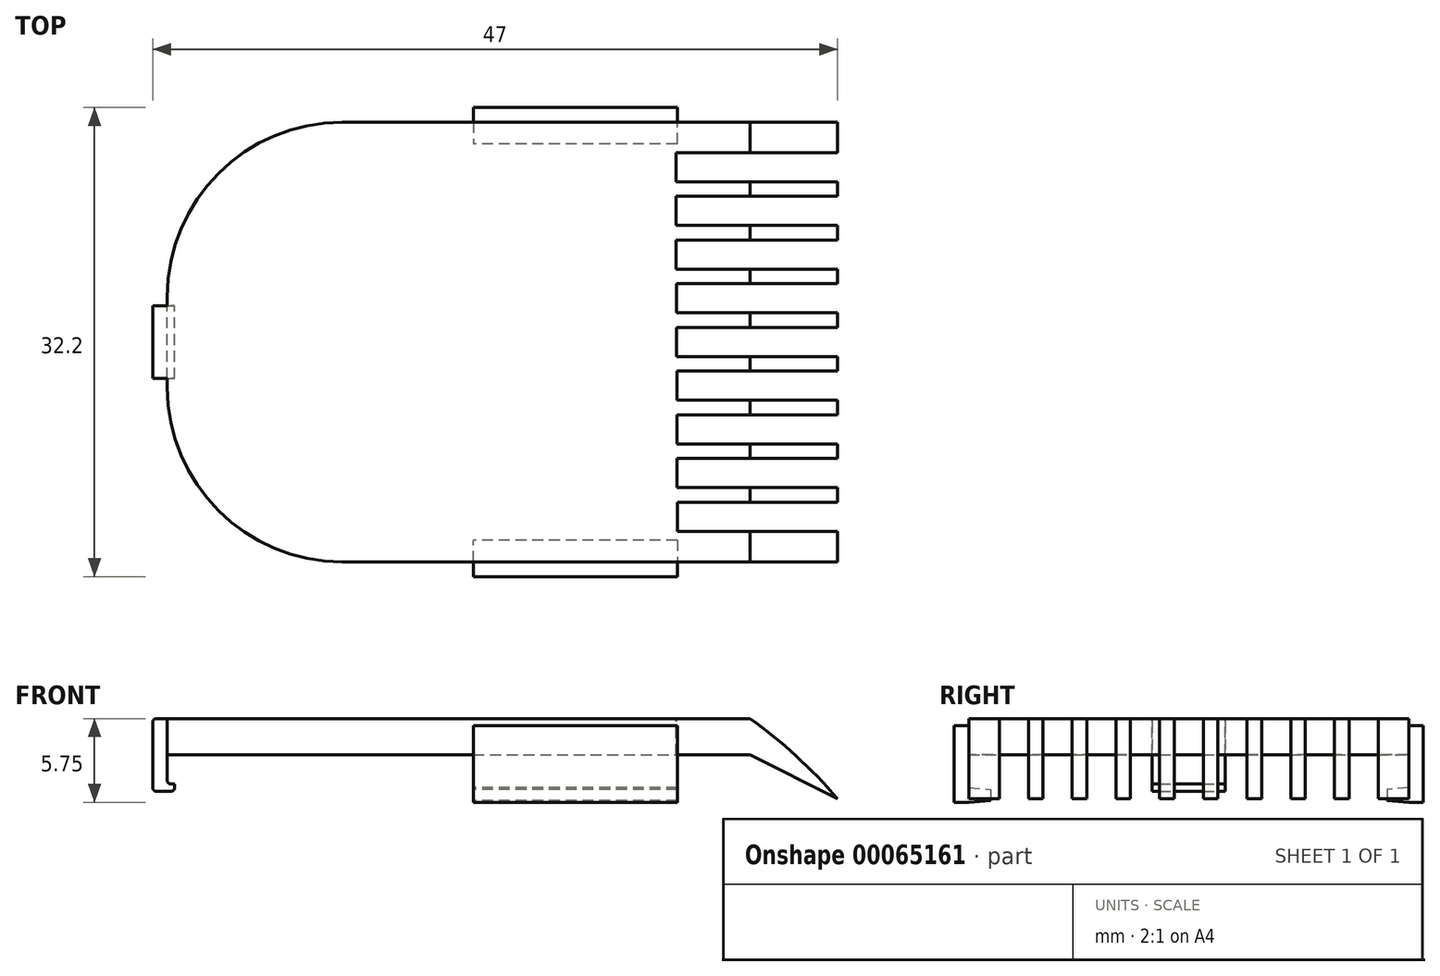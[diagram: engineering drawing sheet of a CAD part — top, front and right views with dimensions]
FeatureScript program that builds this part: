
annotation { "Feature Type Name" : "Feature", "Feature Type Description" : "" }
export const myFeature = defineFeature(function(context is Context, id is Id, definition is map)
    precondition{}
    {
        {
            var Q0;
            Q0=qCreatedBy(makeId("Front.planeOp"),FACE);
            var sketch = newSketch(context, id + "F0", { "sketchPlane" : qUnion([Q0])});
            skLineSegment(sketch, "E0", {"start": v(-71.46, 38.2) * mm, "end": v(-31.46, 38.2) * mm});
            skLineSegment(sketch, "E1", {"start": v(-31.46, 38.2) * mm, "end": v(-25.46, 35.2) * mm});
            skLineSegment(sketch, "E2", {"start": v(-71.46, 38.2) * mm, "end": v(-71.46, 40.7) * mm});
            skLineSegment(sketch, "E3", {"start": v(-71.46, 40.7) * mm, "end": v(-31.46, 40.7) * mm});
            skArc(sketch, "E4", {"start": v(-25.46, 35.2) * mm, "mid": v(-28.3, 38.13) * mm, "end": v(-31.46, 40.7) * mm});
            skLineSegment(sketch, "E5", {"start": v(-71.46, 40.7) * mm, "end": v(-72.21, 40.7) * mm});
            skLineSegment(sketch, "E6", {"start": v(-72.46, 40.45) * mm, "end": v(-72.46, 35.95) * mm});
            skLineSegment(sketch, "E7", {"start": v(-72.21, 35.7) * mm, "end": v(-71.21, 35.7) * mm});
            skLineSegment(sketch, "E8", {"start": v(-70.96, 35.95) * mm, "end": v(-70.96, 36.2) * mm});
            skLineSegment(sketch, "E9", {"start": v(-70.96, 36.2) * mm, "end": v(-71.21, 36.2) * mm});
            skLineSegment(sketch, "E10", {"start": v(-71.46, 36.45) * mm, "end": v(-71.46, 38.2) * mm});
            skPoint(sketch, "E11.visualSharp", {"position": v(-72.46, 40.7) * mm});
            skArc(sketch, "E11.filletArc", {"start": v(-72.21, 40.7) * mm, "mid": v(-72.39, 40.63) * mm, "end": v(-72.46, 40.45) * mm});
            skPoint(sketch, "E12.visualSharp", {"position": v(-72.46, 35.7) * mm});
            skArc(sketch, "E12.filletArc", {"start": v(-72.46, 35.95) * mm, "mid": v(-72.39, 35.77) * mm, "end": v(-72.21, 35.7) * mm});
            skPoint(sketch, "E13.visualSharp", {"position": v(-71.46, 36.2) * mm});
            skArc(sketch, "E13.filletArc", {"start": v(-71.46, 36.45) * mm, "mid": v(-71.39, 36.27) * mm, "end": v(-71.21, 36.2) * mm});
            skPoint(sketch, "E14.visualSharp", {"position": v(-70.96, 35.7) * mm});
            skArc(sketch, "E14.filletArc", {"start": v(-71.21, 35.7) * mm, "mid": v(-71.03, 35.77) * mm, "end": v(-70.96, 35.95) * mm});
            skSolve(sketch);
        }
        {
            var Q0;
            Q0=makeQuery(id+"F0.imprint","IMPRINT",FACE,{"disambiguationData":[TD([[makeQuery(id+"F0.imprint","IMPRINT",EDGE,{"derivedFrom":sQuery(id+"F0.wireOp",EDGE,"E0")}),1.0]])]});
            extrude(context, id + "F1", {"entities" : qUnion([Q0]), "depth" : 15.1 * mm, "hasSecondDirection" : true, "secondDirectionOppositeDirection" : true, "secondDirectionDepth" : 15.1 * mm});
        }
        {
            var Q0;
            Q0=makeQuery(id+"F0.imprint","IMPRINT",FACE,{"disambiguationData":[TD([[makeQuery(id+"F0.imprint","IMPRINT",EDGE,{"derivedFrom":sQuery(id+"F0.wireOp",EDGE,"E2")}),1.0]])]});
            extrude(context, id + "F2", {"entities" : qUnion([Q0]), "operationType" : NewBodyOperationType.ADD, "depth" : 2.5 * mm, "hasSecondDirection" : true, "secondDirectionOppositeDirection" : true, "secondDirectionDepth" : 2.5 * mm});
        }
        {
            var Q0;
            Q0=makeQuery(id+"F1.opExtrude","SWEPT_FACE",FACE,{"disambiguationData":[OSD([sQuery(id+"F0.wireOp",EDGE,"E0")])]});
            var sketch = newSketch(context, id + "F3", { "sketchPlane" : qUnion([Q0])});
            skLineSegment(sketch, "E15", {"start": v(-50.46, -15.1) * mm, "end": v(-50.46, -16.1) * mm});
            skLineSegment(sketch, "E16", {"start": v(-50.46, -16.1) * mm, "end": v(-36.46, -16.1) * mm});
            skLineSegment(sketch, "E17", {"start": v(-36.46, -16.1) * mm, "end": v(-36.46, -15.1) * mm});
            skLineSegment(sketch, "E18", {"start": v(-36.46, -15.1) * mm, "end": v(-50.46, -15.1) * mm});
            skSolve(sketch);
        }
        {
            var Q0;
            {var subQ0=sQuery(id+"F3.wireOp",EDGE,"E15");Q0=makeQuery(id+"F3.imprint","IMPRINT",FACE,{"disambiguationData":[TD([[makeQuery(id+"F3.imprint","IMPRINT",EDGE,{"derivedFrom":subQ0}),1.0]])]});}
            extrude(context, id + "F4", {"entities" : qUnion([Q0]), "oppositeDirection" : true, "depth" : 2 * mm, "hasSecondDirection" : true, "secondDirectionOppositeDirection" : false, "secondDirectionDepth" : 4 * mm});
        }
        {
            var Q0;
            Q0=makeQuery(id+"F4.opExtrude","SWEPT_FACE",FACE,{"disambiguationData":[OSD([sQuery(id+"F3.wireOp",EDGE,"E18")])]});
            var sketch = newSketch(context, id + "F5", { "sketchPlane" : qUnion([Q0])});
            skLineSegment(sketch, "E19", {"start": v(-36.46, 35.95) * mm, "end": v(-50.46, 35.95) * mm});
            skPoint(sketch, "E19.endSnap0", {"position": v(-50.46, 37.2) * mm});
            skLineSegment(sketch, "E20", {"start": v(-43.46, 35.95) * mm, "end": v(-44.46, 34.2) * mm});
            skSolve(sketch);
        }
        {
            var Q0;
            {var subQ0=sQuery(id+"F5.wireOp",EDGE,"E19");Q0=makeQuery(id+"F5.imprint","IMPRINT",FACE,{"disambiguationData":[TD([[makeQuery(id+"F5.imprint","IMPRINT",EDGE,{"derivedFrom":subQ0}),1.0]])]});}
            extrude(context, id + "F6", {"entities" : qUnion([Q0]), "operationType" : NewBodyOperationType.ADD, "depth" : 1.5 * mm});
        }
        {
            var Q0;
            Q0=makeQuery(id+"F2.boolean.opBoolean","MERGE",FACE,{"derivedFrom":[makeQuery(id+"F1.opExtrude","SWEPT_FACE",FACE,{"disambiguationData":[OSD([sQuery(id+"F0.wireOp",EDGE,"E3")])]}),makeQuery(id+"F2.opExtrude","SWEPT_FACE",FACE,{"disambiguationData":[OSD([sQuery(id+"F0.wireOp",EDGE,"E5")])]})]});
            var sketch = newSketch(context, id + "F7", { "sketchPlane" : qUnion([Q0])});
            skLineSegment(sketch, "E21", {"start": v(-23.75, 13) * mm, "end": v(-36.55, 13) * mm});
            skLineSegment(sketch, "E22", {"start": v(-36.55, 13) * mm, "end": v(-36.55, 11) * mm});
            skLineSegment(sketch, "E23", {"start": v(-36.55, 11) * mm, "end": v(-23.68, 11) * mm});
            skLineSegment(sketch, "E24", {"start": v(-23.68, 11) * mm, "end": v(-23.75, 13) * mm});
            skLineSegment(sketch, "E25.1.0.0", {"start": v(-36.54, 8) * mm, "end": v(-23.67, 8) * mm});
            skLineSegment(sketch, "E25.1.0.1", {"start": v(-23.74, 10) * mm, "end": v(-36.54, 10) * mm});
            skLineSegment(sketch, "E25.1.0.2", {"start": v(-36.54, 10) * mm, "end": v(-36.54, 8) * mm});
            skLineSegment(sketch, "E25.1.0.3", {"start": v(-23.67, 8) * mm, "end": v(-23.74, 10) * mm});
            skLineSegment(sketch, "E25.2.0.0", {"start": v(-36.53, 5) * mm, "end": v(-23.66, 5) * mm});
            skLineSegment(sketch, "E25.2.0.1", {"start": v(-23.72, 7) * mm, "end": v(-36.53, 7) * mm});
            skLineSegment(sketch, "E25.2.0.2", {"start": v(-36.53, 7) * mm, "end": v(-36.53, 5) * mm});
            skLineSegment(sketch, "E25.2.0.3", {"start": v(-23.66, 5) * mm, "end": v(-23.72, 7) * mm});
            skLineSegment(sketch, "E25.3.0.0", {"start": v(-36.52, 2) * mm, "end": v(-23.65, 2) * mm});
            skLineSegment(sketch, "E25.3.0.1", {"start": v(-23.71, 4) * mm, "end": v(-36.52, 4) * mm});
            skLineSegment(sketch, "E25.3.0.2", {"start": v(-36.52, 4) * mm, "end": v(-36.52, 2) * mm});
            skLineSegment(sketch, "E25.3.0.3", {"start": v(-23.65, 2) * mm, "end": v(-23.71, 4) * mm});
            skLineSegment(sketch, "E25.4.0.0", {"start": v(-36.5, -1) * mm, "end": v(-23.64, -1) * mm});
            skLineSegment(sketch, "E25.4.0.1", {"start": v(-23.7, 1) * mm, "end": v(-36.5, 1) * mm});
            skLineSegment(sketch, "E25.4.0.2", {"start": v(-36.5, 1) * mm, "end": v(-36.5, -1) * mm});
            skLineSegment(sketch, "E25.4.0.3", {"start": v(-23.64, -1) * mm, "end": v(-23.7, 1) * mm});
            skLineSegment(sketch, "E25.5.0.0", {"start": v(-36.5, -4) * mm, "end": v(-23.63, -4) * mm});
            skLineSegment(sketch, "E25.5.0.1", {"start": v(-23.69, -2) * mm, "end": v(-36.5, -2) * mm});
            skLineSegment(sketch, "E25.5.0.2", {"start": v(-36.5, -2) * mm, "end": v(-36.5, -4) * mm});
            skLineSegment(sketch, "E25.5.0.3", {"start": v(-23.63, -4) * mm, "end": v(-23.69, -2) * mm});
            skLineSegment(sketch, "E25.6.0.0", {"start": v(-36.48, -7) * mm, "end": v(-23.61, -7) * mm});
            skLineSegment(sketch, "E25.6.0.1", {"start": v(-23.68, -5) * mm, "end": v(-36.48, -5) * mm});
            skLineSegment(sketch, "E25.6.0.2", {"start": v(-36.48, -5) * mm, "end": v(-36.48, -7) * mm});
            skLineSegment(sketch, "E25.6.0.3", {"start": v(-23.61, -7) * mm, "end": v(-23.68, -5) * mm});
            skLineSegment(sketch, "E25.7.0.0", {"start": v(-36.47, -10) * mm, "end": v(-23.6, -10) * mm});
            skLineSegment(sketch, "E25.7.0.1", {"start": v(-23.67, -8) * mm, "end": v(-36.47, -8) * mm});
            skLineSegment(sketch, "E25.7.0.2", {"start": v(-36.47, -8) * mm, "end": v(-36.47, -10) * mm});
            skLineSegment(sketch, "E25.7.0.3", {"start": v(-23.6, -10) * mm, "end": v(-23.67, -8) * mm});
            skLineSegment(sketch, "E25.8.0.0", {"start": v(-36.46, -13) * mm, "end": v(-23.6, -13) * mm});
            skLineSegment(sketch, "E25.8.0.1", {"start": v(-23.65, -11) * mm, "end": v(-36.46, -11) * mm});
            skLineSegment(sketch, "E25.8.0.2", {"start": v(-36.46, -11) * mm, "end": v(-36.46, -13) * mm});
            skLineSegment(sketch, "E25.8.0.3", {"start": v(-23.6, -13) * mm, "end": v(-23.65, -11) * mm});
            skLineSegment(sketch, "E25.direction1", {"start": v(-36.55, 11) * mm, "end": v(-36.54, 8) * mm, "construction": true});
            skSolve(sketch);
        }
        {
            var Q0;
            {var subQ0=sQuery(id+"F7.wireOp",EDGE,"E25.8.0.3");Q0=makeQuery(id+"F7.imprint","IMPRINT",FACE,{"disambiguationData":[TD([[makeQuery(id+"F7.imprint","IMPRINT",EDGE,{"derivedFrom":subQ0}),1.0]])]});}
            var Q1;
            {var subQ0=sQuery(id+"F7.wireOp",EDGE,"E25.7.0.3");Q1=makeQuery(id+"F7.imprint","IMPRINT",FACE,{"disambiguationData":[TD([[makeQuery(id+"F7.imprint","IMPRINT",EDGE,{"derivedFrom":subQ0}),1.0]])]});}
            var Q2;
            {var subQ0=sQuery(id+"F7.wireOp",EDGE,"E25.6.0.3");Q2=makeQuery(id+"F7.imprint","IMPRINT",FACE,{"disambiguationData":[TD([[makeQuery(id+"F7.imprint","IMPRINT",EDGE,{"derivedFrom":subQ0}),1.0]])]});}
            var Q3;
            {var subQ0=sQuery(id+"F7.wireOp",EDGE,"E25.5.0.3");Q3=makeQuery(id+"F7.imprint","IMPRINT",FACE,{"disambiguationData":[TD([[makeQuery(id+"F7.imprint","IMPRINT",EDGE,{"derivedFrom":subQ0}),1.0]])]});}
            var Q4;
            {var subQ0=sQuery(id+"F7.wireOp",EDGE,"E25.4.0.3");Q4=makeQuery(id+"F7.imprint","IMPRINT",FACE,{"disambiguationData":[TD([[makeQuery(id+"F7.imprint","IMPRINT",EDGE,{"derivedFrom":subQ0}),1.0]])]});}
            var Q5;
            {var subQ0=sQuery(id+"F7.wireOp",EDGE,"E25.3.0.3");Q5=makeQuery(id+"F7.imprint","IMPRINT",FACE,{"disambiguationData":[TD([[makeQuery(id+"F7.imprint","IMPRINT",EDGE,{"derivedFrom":subQ0}),1.0]])]});}
            var Q6;
            {var subQ0=sQuery(id+"F7.wireOp",EDGE,"E25.2.0.3");Q6=makeQuery(id+"F7.imprint","IMPRINT",FACE,{"disambiguationData":[TD([[makeQuery(id+"F7.imprint","IMPRINT",EDGE,{"derivedFrom":subQ0}),1.0]])]});}
            var Q7;
            {var subQ0=sQuery(id+"F7.wireOp",EDGE,"E25.1.0.3");Q7=makeQuery(id+"F7.imprint","IMPRINT",FACE,{"disambiguationData":[TD([[makeQuery(id+"F7.imprint","IMPRINT",EDGE,{"derivedFrom":subQ0}),1.0]])]});}
            var Q8;
            {var subQ0=sQuery(id+"F7.wireOp",EDGE,"E24");Q8=makeQuery(id+"F7.imprint","IMPRINT",FACE,{"disambiguationData":[TD([[makeQuery(id+"F7.imprint","IMPRINT",EDGE,{"derivedFrom":subQ0}),1.0]])]});}
            var Q9;
            {var subQ0=sQuery(id+"F7.wireOp",EDGE,"E22");Q9=makeQuery(id+"F7.imprint","IMPRINT",FACE,{"disambiguationData":[TD([[makeQuery(id+"F7.imprint","IMPRINT",EDGE,{"derivedFrom":subQ0}),1.0]])]});}
            var Q10;
            {var subQ0=sQuery(id+"F7.wireOp",EDGE,"E25.1.0.2");Q10=makeQuery(id+"F7.imprint","IMPRINT",FACE,{"disambiguationData":[TD([[makeQuery(id+"F7.imprint","IMPRINT",EDGE,{"derivedFrom":subQ0}),1.0]])]});}
            var Q11;
            {var subQ0=sQuery(id+"F7.wireOp",EDGE,"E25.2.0.2");Q11=makeQuery(id+"F7.imprint","IMPRINT",FACE,{"disambiguationData":[TD([[makeQuery(id+"F7.imprint","IMPRINT",EDGE,{"derivedFrom":subQ0}),1.0]])]});}
            var Q12;
            {var subQ0=sQuery(id+"F7.wireOp",EDGE,"E25.3.0.2");Q12=makeQuery(id+"F7.imprint","IMPRINT",FACE,{"disambiguationData":[TD([[makeQuery(id+"F7.imprint","IMPRINT",EDGE,{"derivedFrom":subQ0}),1.0]])]});}
            var Q13;
            {var subQ0=sQuery(id+"F7.wireOp",EDGE,"E25.4.0.2");Q13=makeQuery(id+"F7.imprint","IMPRINT",FACE,{"disambiguationData":[TD([[makeQuery(id+"F7.imprint","IMPRINT",EDGE,{"derivedFrom":subQ0}),1.0]])]});}
            var Q14;
            {var subQ0=sQuery(id+"F7.wireOp",EDGE,"E25.5.0.2");Q14=makeQuery(id+"F7.imprint","IMPRINT",FACE,{"disambiguationData":[TD([[makeQuery(id+"F7.imprint","IMPRINT",EDGE,{"derivedFrom":subQ0}),1.0]])]});}
            var Q15;
            {var subQ0=sQuery(id+"F7.wireOp",EDGE,"E25.6.0.2");Q15=makeQuery(id+"F7.imprint","IMPRINT",FACE,{"disambiguationData":[TD([[makeQuery(id+"F7.imprint","IMPRINT",EDGE,{"derivedFrom":subQ0}),1.0]])]});}
            var Q16;
            {var subQ0=sQuery(id+"F7.wireOp",EDGE,"E25.7.0.2");Q16=makeQuery(id+"F7.imprint","IMPRINT",FACE,{"disambiguationData":[TD([[makeQuery(id+"F7.imprint","IMPRINT",EDGE,{"derivedFrom":subQ0}),1.0]])]});}
            var Q17;
            {var subQ0=sQuery(id+"F7.wireOp",EDGE,"E25.8.0.2");Q17=makeQuery(id+"F7.imprint","IMPRINT",FACE,{"disambiguationData":[TD([[makeQuery(id+"F7.imprint","IMPRINT",EDGE,{"derivedFrom":subQ0}),1.0]])]});}
            extrude(context, id + "F8", {"entities" : qUnion([Q0, Q1, Q2, Q3, Q4, Q5, Q6, Q7, Q8, Q9, Q10, Q11, Q12, Q13, Q14, Q15, Q16, Q17]), "operationType" : NewBodyOperationType.REMOVE, "endBound" : BoundingType.THROUGH_ALL, "oppositeDirection" : true, "depth" : 25 * mm});
        }
        {
            var Q0;
            {var subQ0=sQuery(id+"F3.wireOp",EDGE,"E15");Q0=makeQuery(id+"F6.boolean.opBoolean","MERGE",FACE,{"derivedFrom":[makeQuery(id+"F4.opExtrude","SWEPT_FACE",FACE,{"disambiguationData":[OSD([subQ0])]}),makeQuery(id+"F6.opExtrude","SWEPT_FACE",FACE,{"disambiguationData":[OSD([sQuery(id+"F0.wireOp",EDGE,"E0"),subQ0,sQuery(id+"F3.wireOp",EDGE,"E18")])]})]});}
            var sketch = newSketch(context, id + "F9", { "sketchPlane" : qUnion([Q0])});
            skLineSegment(sketch, "E26", {"start": v(-16.1, 34.95) * mm, "end": v(-13.6, 34.95) * mm});
            skLineSegment(sketch, "E27", {"start": v(-15.1, 35.95) * mm, "end": v(-13.6, 35.82) * mm});
            skLineSegment(sketch, "E28", {"start": v(-13.6, 34.95) * mm, "end": v(-13.6, 35.95) * mm});
            skLineSegment(sketch, "E29", {"start": v(-13.6, 35.45) * mm, "end": v(-16.1, 35.45) * mm});
            skLineSegment(sketch, "E30.MirrorCS", {"start": v(-15.1, 34.95) * mm, "end": v(-13.6, 35.07) * mm});
            skSolve(sketch);
        }
        {
            var Q0;
            {var subQ0=sQuery(id+"F9.wireOp",EDGE,"E27");Q0=makeQuery(id+"F9.imprint","IMPRINT",FACE,{"disambiguationData":[TD([[makeQuery(id+"F9.imprint","IMPRINT",EDGE,{"derivedFrom":subQ0}),1.0]])]});}
            var Q1;
            {var subQ3=sQuery(id+"F9.wireOp",EDGE,"E30.MirrorCS");Q1=makeQuery(id+"F9.imprint","IMPRINT",FACE,{"disambiguationData":[TD([[makeQuery(id+"F9.imprint","IMPRINT",EDGE,{"derivedFrom":subQ3}),-1.0]])]});}
            var Q2;
            {var subQ0=sQuery(id+"F3.wireOp",EDGE,"E18");var subQ1=sQuery(id+"F3.wireOp",EDGE,"E15");var subQ2=sQuery(id+"F0.wireOp",EDGE,"E0");var subQ3=makeQuery(id+"F6.boolean.opBoolean","MERGE",EDGE,{"derivedFrom":[makeQuery(id+"F4.opExtrude","CAP_EDGE",EDGE,{"disambiguationData":[OSD([subQ1])],"isStart":true}),makeQuery(id+"F6.opExtrude","SWEPT_EDGE",EDGE,{"disambiguationData":[OSD([subQ2,subQ1,subQ0])]})]});Q2=makeQuery(id+"F9.imprint","IMPRINT",FACE,{"disambiguationData":[TD([[makeQuery(id+"F9.imprint","IMPRINT",EDGE,{"derivedFrom":subQ3}),-1.0]])]});}
            extrude(context, id + "F10", {"entities" : qUnion([Q0, Q1, Q2]), "operationType" : NewBodyOperationType.REMOVE, "oppositeDirection" : true, "depth" : 15 * mm});
        }
        {
            var Q0;
            Q0=makeQuery(id+"F1.opExtrude","CAP_EDGE",EDGE,{"disambiguationData":[OSD([sQuery(id+"F0.wireOp",EDGE,"E2")])],"isStart":false});
            var Q1;
            Q1=makeQuery(id+"F1.opExtrude","CAP_EDGE",EDGE,{"disambiguationData":[OSD([sQuery(id+"F0.wireOp",EDGE,"E2")])],"isStart":true});
            fillet(context, id + "F11", {"entities" : qUnion([Q0, Q1]), "radius" : 12 * mm, "tangentPropagation" : true, "allowEdgeOverflow" : false});
        }
        {
            var Q0;
            Q0=makeQuery(id+"F4.opExtrude","SWEPT_BODY",BODY,{"disambiguationData":[OSD([sQuery(id+"F3.wireOp",EDGE,"E15"),sQuery(id+"F3.wireOp",EDGE,"E16"),sQuery(id+"F3.wireOp",EDGE,"E17"),sQuery(id+"F3.wireOp",EDGE,"E18")])]});
            var Q1;
            Q1=qCreatedBy(makeId("Front.planeOp"),FACE);
            mirror(context, id + "F12", {"operationType" : NewBodyOperationType.ADD, "entities" : qUnion([Q0]), "mirrorPlane" : qUnion([Q1])});
        }
    });
